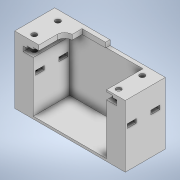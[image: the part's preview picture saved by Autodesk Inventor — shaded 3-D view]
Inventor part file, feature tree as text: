
AUTODESK INVENTOR PART (.ipt)
format: ipt  version: 2022 (Build 260153000, 153)  size: 335,360 bytes
history: native  units: mm
features: sketch x9, extrude x8, other x5, fillet x2, mirror x1
ambient origin geometry x8: Origin, YZ Plane, XZ Plane, XY Plane, X Axis, Y Axis, Z Axis, Center Point
bodies: Body1 (feature_tree)
feature tree (25):
  other  "Твердое тело1"
  extrude  "Выдавливание1"  Depth=29.25mm
  extrude  "Выдавливание2"  Depth=59.05mm
  extrude  "Выдавливание3"  Depth=15.0mm
  other  "РабПлоскость1"
  extrude  "Выдавливание4"  Depth=3.0mm
  other  "РабПлоскость2"
  other  "РабПлоскость3"
  other  "РабПлоскость5"
  extrude  "Выдавливание10"  Depth=41.0mm TaperAngle=0.0deg
  extrude  "Выдавливание11"  Depth=2.0mm TaperAngle=0.0deg
  fillet  "Сопряжение8"  Radius=4.2mm
  extrude  "Выдавливание12"  Depth=20.0mm TaperAngle=0.0deg
  fillet  "Сопряжение9"  [1 undecoded]
  mirror  "Зеркальное отражение2"
  extrude  "Выдавливание13"  Depth=7.15mm
  sketch  "Эскиз14"
  sketch  "Эскиз1"
  sketch  "Эскиз2"
  sketch  "Эскиз3"
  sketch  "Эскиз4"
  sketch  "Эскиз10"
  sketch  "Эскиз11"
  sketch  "Эскиз13"
  sketch  "Эскиз15"
note: 1 required parameter value undecoded (feature->parameter linkage not recoverable at this tier; creation-order binding heuristic only, values carry confidence <= 0.55)
